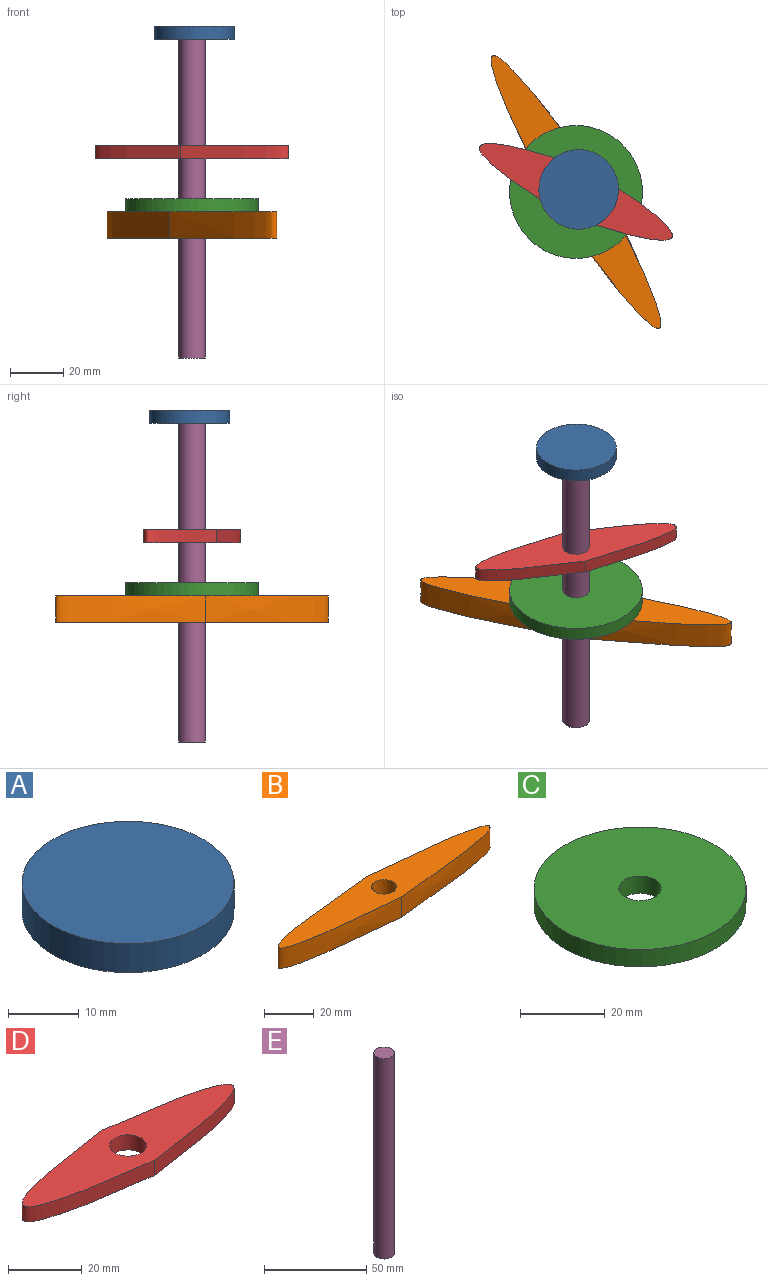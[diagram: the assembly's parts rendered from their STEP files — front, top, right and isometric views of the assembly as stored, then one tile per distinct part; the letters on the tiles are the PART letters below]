
ASSEMBLY  parts=5 mates=4
PART A: 3 faces, bbox 30x30x5 mm
  f0: cylinder r=15mm len=30mm, axis (0,0,-1), area 471.2mm2, adj f1,f2
  f1: plane 30x30mm, normal (0,0,1), area 706.9mm2, adj f0
  f2: plane 30x30mm, normal (0,0,-1), area 706.9mm2, adj f0
PART B: 5 faces, bbox 165x20x10 mm
  f0: extruded ~60x20mm, area 1231.1mm2, adj f1,f2,f3
  f1: extruded ~60x20mm, area 1231.1mm2, adj f0,f2,f3
  f2: plane 165x20mm, normal (0,0,1), area 1521.5mm2, adj f0,f1,f4
  f3: plane 165x20mm, normal (0,0,-1), area 1521.5mm2, adj f0,f1,f4
  f4: cylinder r=5mm len=10mm, axis (0,0,-1), area 314.2mm2, adj f2,f3
PART C: 4 faces, bbox 50x50x5 mm
  f0: cylinder r=25mm len=50mm, axis (0,0,-1), area 785.4mm2, adj f1,f2
  f1: plane 50x50mm, normal (0,0,1), area 1885mm2, adj f0,f3
  f2: plane 50x50mm, normal (0,0,-1), area 1885mm2, adj f0,f3
  f3: cylinder r=5mm len=10mm, axis (0,0,-1), area 157.1mm2, adj f1,f2
PART D: 5 faces, bbox 110x20x5 mm
  f0: extruded ~40x20mm, area 420.5mm2, adj f1,f2,f3
  f1: extruded ~40x20mm, area 420.5mm2, adj f0,f2,f3
  f2: plane 110x20mm, normal (0,0,-1), area 988.1mm2, adj f0,f1,f4
  f3: plane 110x20mm, normal (0,0,1), area 988.1mm2, adj f0,f1,f4
  f4: cylinder r=5mm len=10mm, axis (0,0,1), area 157.1mm2, adj f2,f3
PART E: 3 faces, bbox 10x10x120 mm
  f0: cylinder r=5mm len=120mm, axis (0,0,-1), area 3769.9mm2, adj f1,f2
  f1: plane 10x10mm, normal (0,0,1), area 78.5mm2, adj f0
  f2: plane 10x10mm, normal (0,0,-1), area 78.5mm2, adj f0
PLACE A rot(axis=(0,0,1),142.7deg) t=(1.02,0.85,0)mm
PLACE B rot(axis=(0,0,1),121.5deg) t=(0,0,-5)mm
PLACE C t=(0,0,55)mm
PLACE D rot(axis=(0,0,1),154.8deg) t=(0,0,55)mm
PLACE E at identity fixed
MATE fastened C.f0 <-> E.f0  axis (0,0,1) through (0,0,60)mm
MATE planar E.f0 <-> A.f0  axis (0,0,1) through (0,0,120)mm
MATE revolute E.f0 <-> D.f4  axis (0,0,-1) through (0,0,120)mm
MATE cylindrical E.f0 <-> B.f4  axis (0,0,-1) through (0,0,0)mm
